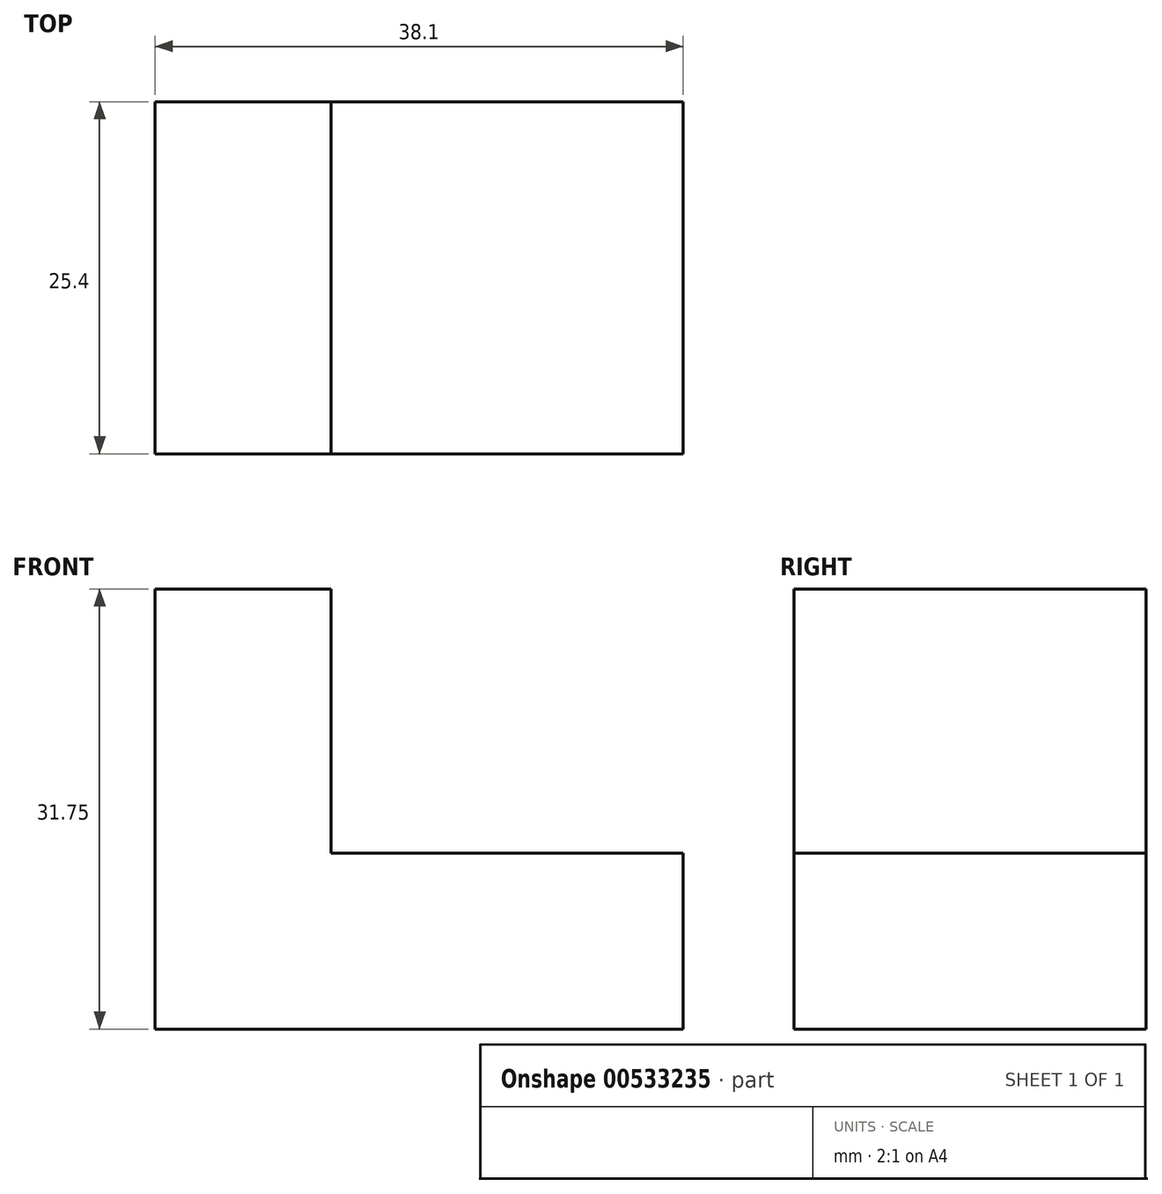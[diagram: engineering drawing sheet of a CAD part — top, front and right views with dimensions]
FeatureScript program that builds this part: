
annotation { "Feature Type Name" : "Feature", "Feature Type Description" : "" }
export const myFeature = defineFeature(function(context is Context, id is Id, definition is map)
    precondition{}
    {
        {
            var Q0;
            Q0=qCreatedBy(makeId("Front.planeOp"),FACE);
            var sketch = newSketch(context, id + "F0", { "sketchPlane" : qUnion([Q0])});
            skLineSegment(sketch, "E0", {"start": v(-57.6, 33.08) * mm, "end": v(-44.9, 33.08) * mm});
            skLineSegment(sketch, "E1", {"start": v(-57.6, 33.08) * mm, "end": v(-57.6, 1.33) * mm});
            skLineSegment(sketch, "E2", {"start": v(-57.6, 1.33) * mm, "end": v(-19.5, 1.33) * mm});
            skLineSegment(sketch, "E3", {"start": v(-44.9, 33.08) * mm, "end": v(-44.9, 14.03) * mm});
            skLineSegment(sketch, "E4", {"start": v(-44.9, 14.03) * mm, "end": v(-19.5, 14.03) * mm});
            skLineSegment(sketch, "E5", {"start": v(-19.5, 14.03) * mm, "end": v(-19.5, 1.33) * mm});
            skSolve(sketch);
        }
        {
            var Q0;
            Q0 = qSketchRegion(id + "F0", true);
            extrude(context, id + "F1", {"entities" : qUnion([Q0]), "depth" : 25.4 * mm, "offsetDistance" : 25.4 * mm});
        }
    });
